# Revit family: NLRS_74_PF_UN_bad_S8H1D000000_SPHINX_BCB
name_source: partatom
category: Plumbing Fixtures
revit_build: Autodesk Revit 2016 (Build: 20150220_1215(x64)
units: mm (PartAtom-declared; Revit-internal decimal feet)

## family parameters
Always vertical = Yes
Cut with Voids When Loaded = No
OmniClass Number = 23.45.00.00
OmniClass Title = Sanitary, Laundry, and Cleaning Equipment
Part Type = Normal
Room Calculation Point = No
Round Connector Dimension = Use Radius
Shared = No
Work Plane-Based = No

## types (1)
- 420 bad 170x75
    74_kunststof = <By Category>
    Assembly Code = 4(74.11)
    Description = bad
    IfcElement = IfcFlowTerminal
    IfcExportAs = IfcSanitaryTerminalTypeEnum
    IfcExportType = BATH
    IfcTypeProduct = IfcSanitaryTerminalType
    Keynote = bad
    Manufacturer = Sphinx
    Material = kunststof
    Model = 420 bad 170x75
    NLRS_C_URL_BCB = http://bcb-online.nl
    NLRS_C_breedte = 750 mm  [stored 2.46063 ft]
    NLRS_C_code_EAN = 8711754032361
    NLRS_C_code_artikel = S8H1B000000
    NLRS_C_content_datum_gewijzigd = APR-2018
    NLRS_C_content_datum_uitgifte = APR-2018
    NLRS_C_content_provider = BouwConnect
    NLRS_C_content_versie = 2.0
    NLRS_C_diameter_uit = 50 mm  [stored 0.164042 ft]
    NLRS_C_hoogte = 470 mm  [stored 1.54199 ft]
    NLRS_C_lengte = 1700 mm  [stored 5.57743 ft]
    NLRS_C_materiaal = NLRS_n6_acryl_wit_Sphinx
    NLRS_C_materiaal_01 = NLRS_h2_staal_Sphinx
    NLRS_C_revit_versie = 2016
    NLRS_S_gewicht = 0.00 kg
    URL = http://www.sphinx.nl
    WFU = 0
    artikelnummer = S8H1D000000
    breedte = 750 mm  [stored 2.46063 ft]
    code_EAN = 8711754226777
    hoogte = 470 mm  [stored 1.54199 ft]
    kleur = wit
    lengte = 1700 mm  [stored 5.57743 ft]
    radius = 25 mm  [stored 0.082021 ft]

note: [stored X ft] marks values corroborated as IEEE doubles in the binary element streams (Revit-internal decimal feet)

## geometry (parser evidence)
native form markers: Sweep x3
no freeform markers — native parametric forms only
